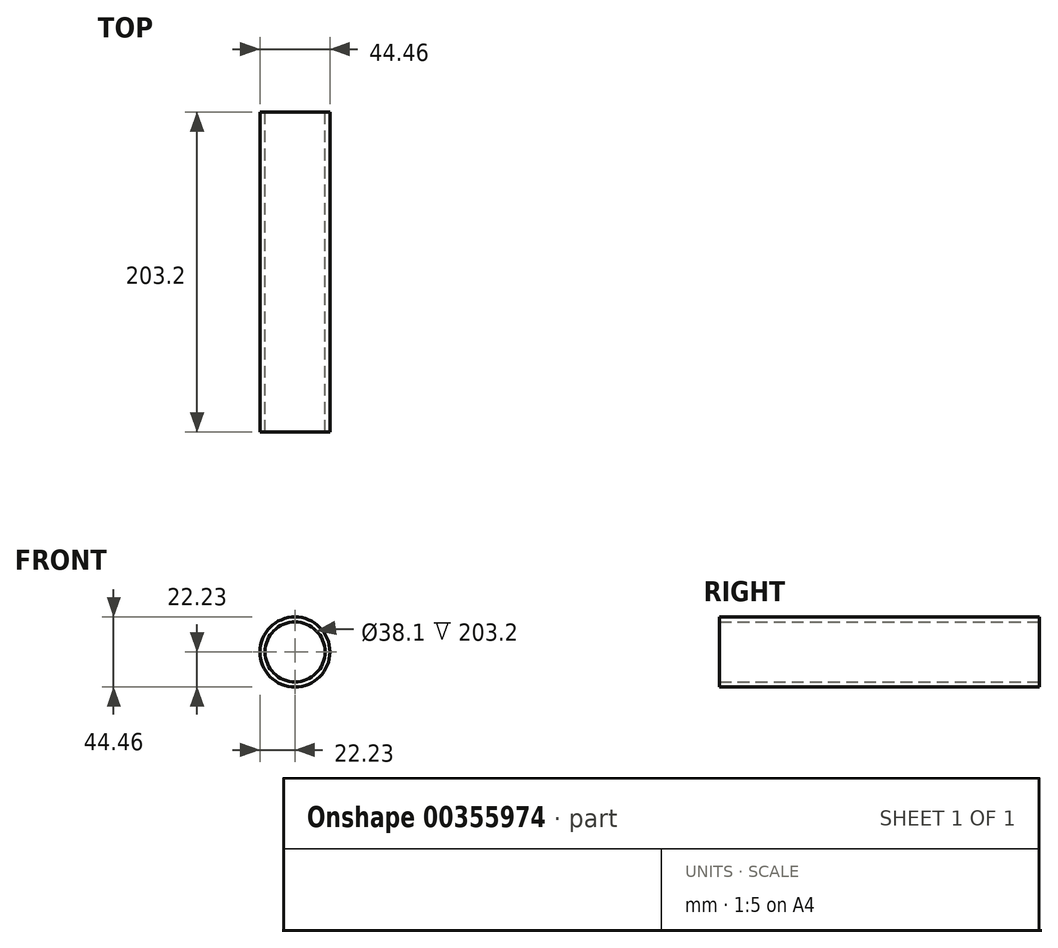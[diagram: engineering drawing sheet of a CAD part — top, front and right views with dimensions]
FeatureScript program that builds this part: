
annotation { "Feature Type Name" : "Feature", "Feature Type Description" : "" }
export const myFeature = defineFeature(function(context is Context, id is Id, definition is map)
    precondition{}
    {
        {
            var Q0;
            Q0=qCreatedBy(makeId("Front.planeOp"),FACE);
            var sketch = newSketch(context, id + "F0", { "sketchPlane" : qUnion([Q0])});
            skCircle(sketch, "E0", {"center": v(0, 0) * mm, "radius": 19.05 * mm});
            skCircle(sketch, "E1", {"center": v(0, 0) * mm, "radius": 22.23 * mm});
            skSolve(sketch);
        }
        {
            var Q0;
            Q0=makeQuery(id+"F0.imprint","IMPRINT",FACE,{"disambiguationData":[TD([[makeQuery(id+"F0.imprint","IMPRINT",EDGE,{"derivedFrom":sQuery(id+"F0.wireOp",EDGE,"E0")}),-1.0]])]});
            extrude(context, id + "F1", {"entities" : qUnion([Q0]), "depth" : 203.2 * mm});
        }
    });
